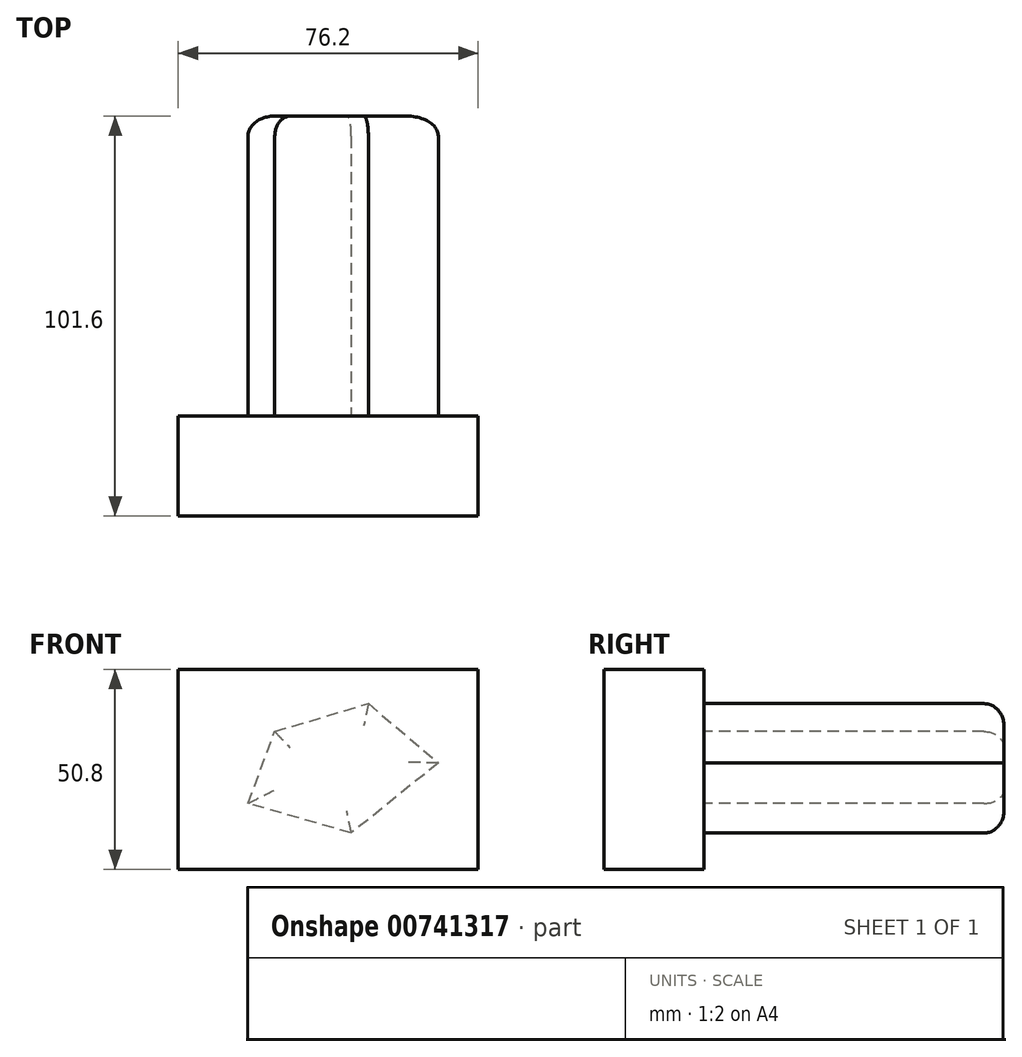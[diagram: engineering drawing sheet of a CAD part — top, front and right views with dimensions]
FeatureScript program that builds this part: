
annotation { "Feature Type Name" : "Feature", "Feature Type Description" : "" }
export const myFeature = defineFeature(function(context is Context, id is Id, definition is map)
    precondition{}
    {
        {
            var Q0;
            Q0=qCreatedBy(makeId("Front.planeOp"),FACE);
            var sketch = newSketch(context, id + "F0", { "sketchPlane" : qUnion([Q0])});
            skLineSegment(sketch, "E0.bottom", {"start": v(0, 0) * mm, "end": v(76.2, 0) * mm});
            skLineSegment(sketch, "E0.top", {"start": v(0, 50.8) * mm, "end": v(76.2, 50.8) * mm});
            skLineSegment(sketch, "E0.left", {"start": v(0, 0) * mm, "end": v(0, 50.8) * mm});
            skLineSegment(sketch, "E0.right", {"start": v(76.2, 0) * mm, "end": v(76.2, 50.8) * mm});
            skSolve(sketch);
        }
        {
            var Q0;
            Q0=makeQuery(id+"F0.imprint","IMPRINT",FACE,{"disambiguationData":[TD([[makeQuery(id+"F0.imprint","IMPRINT",EDGE,{"derivedFrom":sQuery(id+"F0.wireOp",EDGE,"E0.bottom")}),1.0]])]});
            extrude(context, id + "F1", {"entities" : qUnion([Q0]), "depth" : 25.4 * mm, "offsetDistance" : 25.4 * mm});
        }
        {
            var Q0;
            Q0=makeQuery(id+"F1.opExtrude","CAP_FACE",FACE,{"disambiguationData":[OSD([sQuery(id+"F0.wireOp",EDGE,"E0.bottom"),sQuery(id+"F0.wireOp",EDGE,"E0.top"),sQuery(id+"F0.wireOp",EDGE,"E0.left"),sQuery(id+"F0.wireOp",EDGE,"E0.right")])],"isStart":true});
            var sketch = newSketch(context, id + "F2", { "sketchPlane" : qUnion([Q0])});
            skLineSegment(sketch, "E1", {"start": v(-17.74, 16.77) * mm, "end": v(-24.53, 35.03) * mm});
            skLineSegment(sketch, "E2", {"start": v(-24.53, 35.03) * mm, "end": v(-48.32, 42.13) * mm});
            skLineSegment(sketch, "E3", {"start": v(-48.32, 42.13) * mm, "end": v(-66.1, 27.07) * mm});
            skLineSegment(sketch, "E4", {"start": v(-66.1, 27.07) * mm, "end": v(-43.98, 9.24) * mm});
            skLineSegment(sketch, "E5", {"start": v(-43.98, 9.24) * mm, "end": v(-17.74, 16.77) * mm});
            skSolve(sketch);
        }
        {
            var Q0;
            Q0=makeQuery(id+"F2.imprint","IMPRINT",FACE,{"disambiguationData":[TD([[makeQuery(id+"F2.imprint","IMPRINT",EDGE,{"derivedFrom":sQuery(id+"F2.wireOp",EDGE,"E1")}),1.0]])]});
            extrude(context, id + "F3", {"entities" : qUnion([Q0]), "operationType" : NewBodyOperationType.ADD, "depth" : 76.2 * mm, "offsetDistance" : 25.4 * mm});
        }
        {
            var Q0;
            Q0=makeQuery(id+"F3.opExtrude","CAP_EDGE",EDGE,{"disambiguationData":[OSD([sQuery(id+"F2.wireOp",EDGE,"E4")])],"isStart":false});
            var Q1;
            Q1=makeQuery(id+"F3.opExtrude","CAP_EDGE",EDGE,{"disambiguationData":[OSD([sQuery(id+"F2.wireOp",EDGE,"E5")])],"isStart":false});
            var Q2;
            Q2=makeQuery(id+"F3.opExtrude","CAP_EDGE",EDGE,{"disambiguationData":[OSD([sQuery(id+"F2.wireOp",EDGE,"E1")])],"isStart":false});
            var Q3;
            Q3=makeQuery(id+"F3.opExtrude","CAP_EDGE",EDGE,{"disambiguationData":[OSD([sQuery(id+"F2.wireOp",EDGE,"E2")])],"isStart":false});
            var Q4;
            Q4=makeQuery(id+"F3.opExtrude","CAP_EDGE",EDGE,{"disambiguationData":[OSD([sQuery(id+"F2.wireOp",EDGE,"E3")])],"isStart":false});
            fillet(context, id + "F4", {"entities" : qUnion([Q0, Q1, Q2, Q3, Q4]), "radius" : 5.08 * mm, "tangentPropagation" : true, "allowEdgeOverflow" : false});
        }
    });
